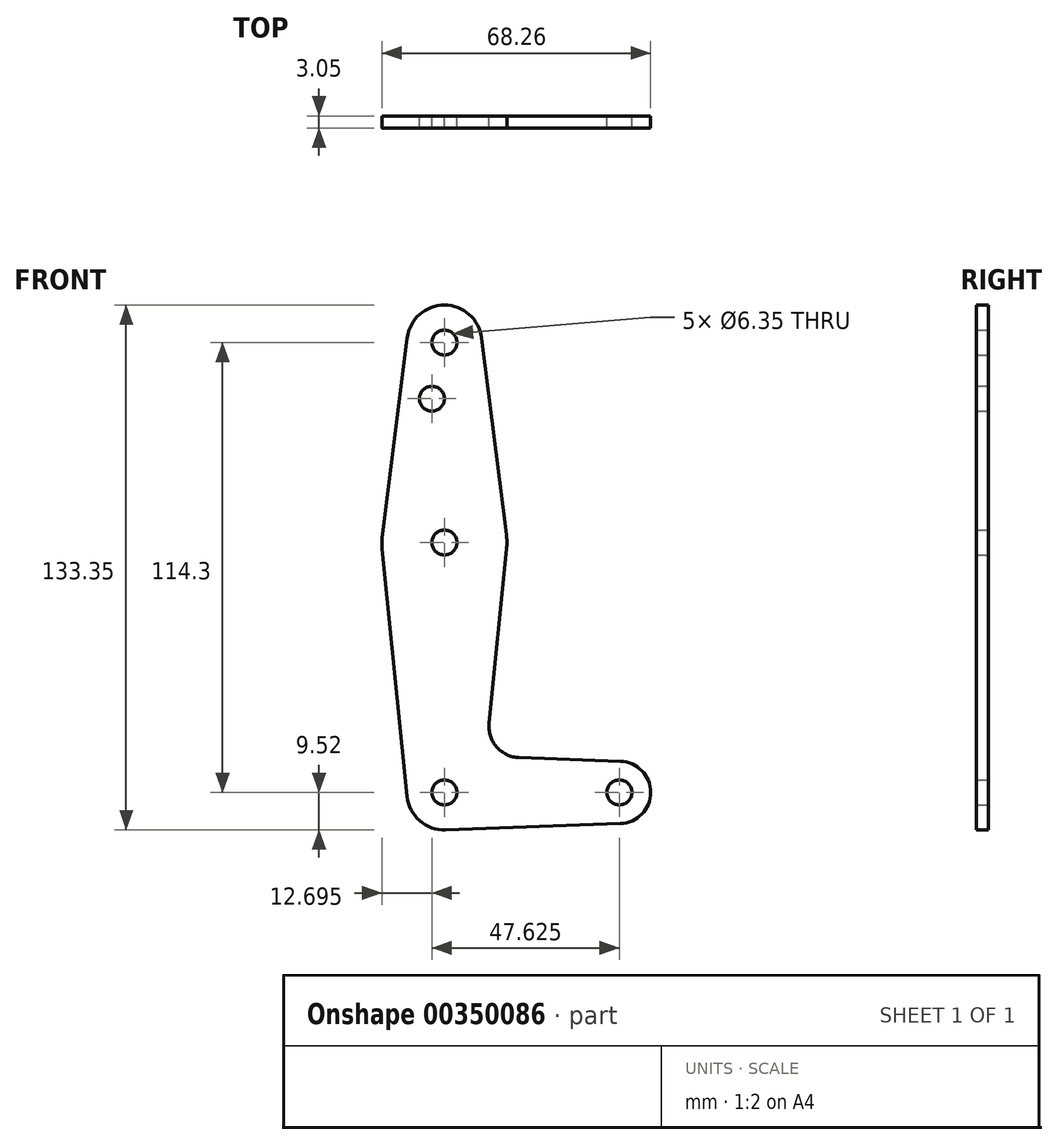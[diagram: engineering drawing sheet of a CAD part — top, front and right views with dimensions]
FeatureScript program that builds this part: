
annotation { "Feature Type Name" : "Feature", "Feature Type Description" : "" }
export const myFeature = defineFeature(function(context is Context, id is Id, definition is map)
    precondition{}
    {
        {
            var Q0;
            Q0=qCreatedBy(makeId("Front.planeOp"),FACE);
            var sketch = newSketch(context, id + "F0", { "sketchPlane" : qUnion([Q0])});
            skCircle(sketch, "E0", {"center": v(0, 0) * mm, "radius": 9.53 * mm});
            skCircle(sketch, "E1", {"center": v(0, 114.3) * mm, "radius": 9.53 * mm});
            skCircle(sketch, "E2", {"center": v(0, 63.5) * mm, "radius": 15.88 * mm});
            skCircle(sketch, "E3", {"center": v(44.45, 0) * mm, "radius": 7.94 * mm});
            skLineSegment(sketch, "E4", {"start": v(0, 114.3) * mm, "end": v(0, 0) * mm, "construction": true});
            skLineSegment(sketch, "E5", {"start": v(0, 0) * mm, "end": v(44.45, 0) * mm, "construction": true});
            skLineSegment(sketch, "E6", {"start": v(18.97, 8.85) * mm, "end": v(44.73, 7.93) * mm});
            skLineSegment(sketch, "E7", {"start": v(0.34, -9.52) * mm, "end": v(44.73, -7.93) * mm});
            skCircle(sketch, "E8", {"center": v(0, 114.3) * mm, "radius": 3.18 * mm});
            skCircle(sketch, "E9", {"center": v(0, 63.5) * mm, "radius": 3.18 * mm});
            skCircle(sketch, "E10", {"center": v(-3.17, 100.03) * mm, "radius": 3.18 * mm});
            skCircle(sketch, "E11", {"center": v(0, 0) * mm, "radius": 3.18 * mm});
            skCircle(sketch, "E12", {"center": v(44.45, 0) * mm, "radius": 3.18 * mm});
            skLineSegment(sketch, "E13", {"start": v(-9.45, 115.5) * mm, "end": v(-15.75, 65.48) * mm});
            skLineSegment(sketch, "E14", {"start": v(9.45, 115.5) * mm, "end": v(15.75, 65.48) * mm});
            skLineSegment(sketch, "E15", {"start": v(15.8, 61.91) * mm, "end": v(11.34, 17.6) * mm});
            skLineSegment(sketch, "E16", {"start": v(-15.8, 61.91) * mm, "end": v(-9.48, -0.95) * mm});
            skArc(sketch, "E17.filletArc", {"start": v(11.34, 17.6) * mm, "mid": v(13.26, 11.57) * mm, "end": v(18.97, 8.85) * mm});
            skSolve(sketch);
        }
        {
            var Q0;
            Q0=makeQuery(id+"F0.imprint","IMPRINT",FACE,{"disambiguationData":[TD([[makeQuery(id+"F0.imprint","IMPRINT",EDGE,{"derivedFrom":sQuery(id+"F0.wireOp",EDGE,"E8")}),-1.0]])]});
            var Q1;
            {var subQ0=sQuery(id+"F0.wireOp",EDGE,"rsqXAEXr-db0p-xM5L-kRlw-wV5Hfu89kmjG");Q1=makeQuery(id+"F0.imprint","IMPRINT",FACE,{"disambiguationData":[TD([[makeQuery(id+"F0.imprint","IMPRINT",EDGE,{"derivedFrom":subQ0}),1.0]])]});}
            var Q2;
            Q2=makeQuery(id+"F0.imprint","IMPRINT",FACE,{"disambiguationData":[TD([[makeQuery(id+"F0.imprint","IMPRINT",EDGE,{"derivedFrom":sQuery(id+"F0.wireOp",EDGE,"E9")}),-1.0]])]});
            var Q3;
            {var subQ6=sQuery(id+"F0.wireOp",EDGE,"E6");Q3=makeQuery(id+"F0.imprint","IMPRINT",FACE,{"disambiguationData":[TD([[makeQuery(id+"F0.imprint","IMPRINT",EDGE,{"derivedFrom":subQ6}),-1.0]])]});}
            var Q4;
            Q4=makeQuery(id+"F0.imprint","IMPRINT",FACE,{"disambiguationData":[TD([[makeQuery(id+"F0.imprint","IMPRINT",EDGE,{"derivedFrom":sQuery(id+"F0.wireOp",EDGE,"E11")}),-1.0]])]});
            var Q5;
            Q5=makeQuery(id+"F0.imprint","IMPRINT",FACE,{"disambiguationData":[TD([[makeQuery(id+"F0.imprint","IMPRINT",EDGE,{"derivedFrom":sQuery(id+"F0.wireOp",EDGE,"E12")}),-1.0]])]});
            var Q6;
            Q6=makeQuery(id+"F0.imprint","IMPRINT",FACE,{"disambiguationData":[TD([[makeQuery(id+"F0.imprint","IMPRINT",EDGE,{"derivedFrom":sQuery(id+"F0.wireOp",EDGE,"E10")}),-1.0]])]});
            extrude(context, id + "F1", {"entities" : qUnion([Q0, Q1, Q2, Q3, Q4, Q5, Q6]), "depth" : 3.05 * mm});
        }
    });
